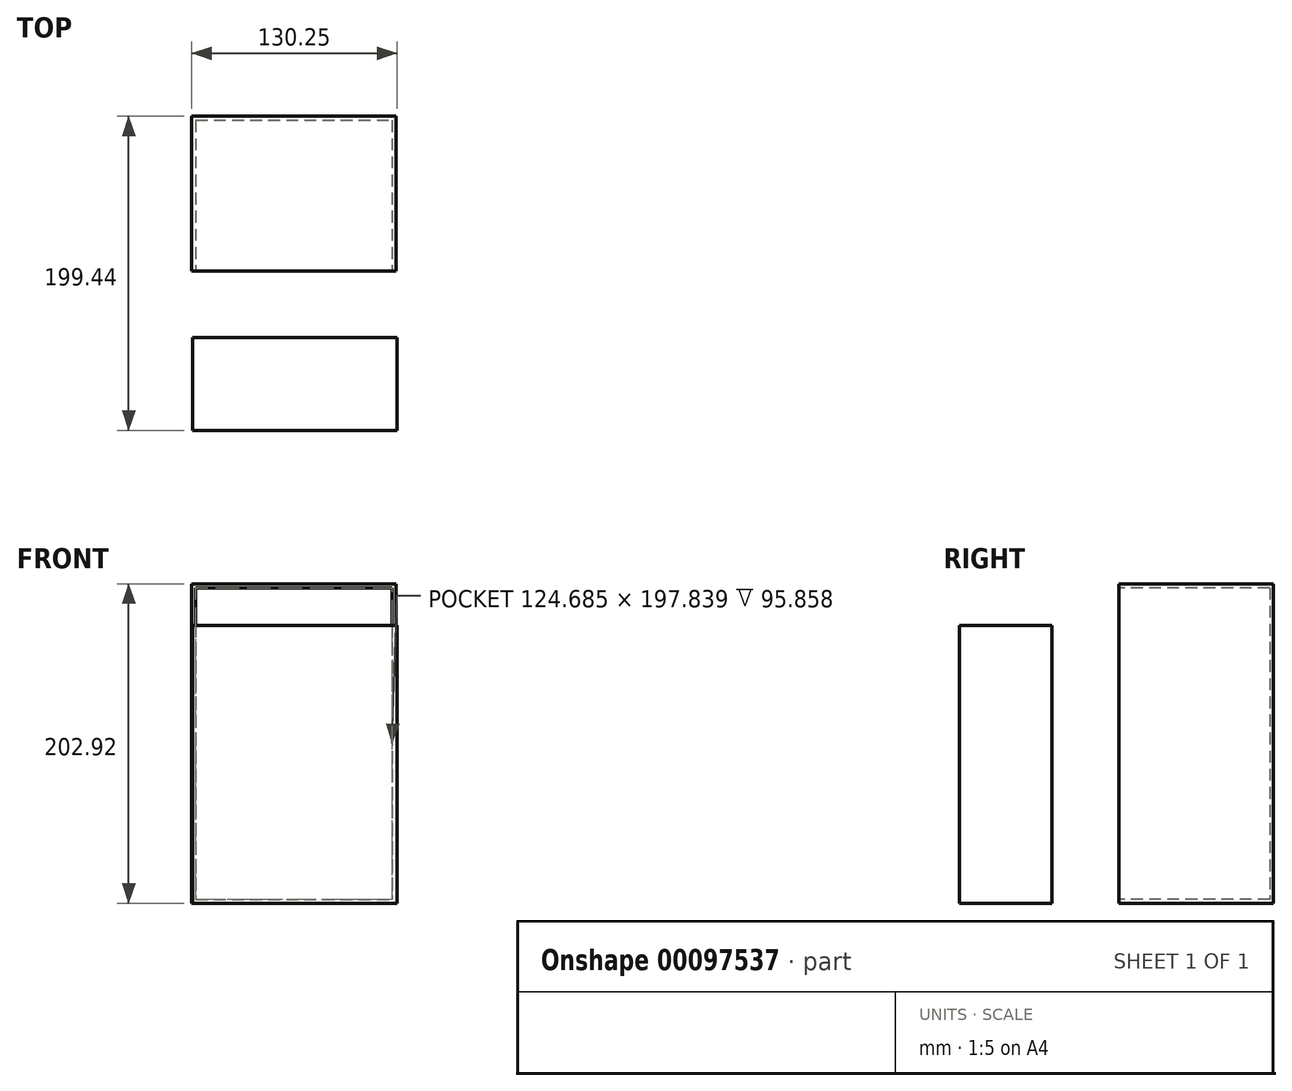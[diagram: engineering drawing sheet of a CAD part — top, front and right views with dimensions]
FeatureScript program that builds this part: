
annotation { "Feature Type Name" : "Feature", "Feature Type Description" : "" }
export const myFeature = defineFeature(function(context is Context, id is Id, definition is map)
    precondition{}
    {
        {
            var Q0;
            Q0=qCreatedBy(makeId("Top.planeOp"),FACE);
            var sketch = newSketch(context, id + "F5", { "sketchPlane" : qUnion([Q0])});
            skLineSegment(sketch, "E0.bottom", {"start": v(-37, 0) * mm, "end": v(92.76, 0) * mm});
            skLineSegment(sketch, "E0.top", {"start": v(-37, -98.4) * mm, "end": v(92.76, -98.4) * mm});
            skLineSegment(sketch, "E0.left", {"start": v(-37, 0) * mm, "end": v(-37, -98.4) * mm});
            skLineSegment(sketch, "E0.right", {"start": v(92.76, 0) * mm, "end": v(92.76, -98.4) * mm});
            skSolve(sketch);
        }
        {
            var Q0;
            Q0=makeQuery(id+"F5.imprint","IMPRINT",FACE,{"disambiguationData":[TD([[makeQuery(id+"F5.imprint","IMPRINT",EDGE,{"derivedFrom":sQuery(id+"F5.wireOp",EDGE,"E0.bottom")}),-1.0]])]});
            var sketch = newSketch(context, id + "F0", { "sketchPlane" : qUnion([Q0])});
            skSolve(sketch);
        }
        {
            var Q0;
            Q0 = qSketchRegion(id + "F0", true);
            var Q1;
            Q1=makeQuery(id+"F0.imprint","IMPRINT",FACE,{"disambiguationData":[TD([[makeQuery(id+"F0.imprint","IMPRINT",EDGE,{"derivedFrom":makeQuery(id+"F5.imprint","IMPRINT",EDGE,{"derivedFrom":sQuery(id+"F5.wireOp",EDGE,"E0.bottom")})}),-1.0]])]});
            extrude(context, id + "F1", {"entities" : qUnion([Q0, Q1]), "depth" : 202.92 * mm});
        }
        {
            var Q0;
            Q0=makeQuery(id+"F1.opExtrude","SWEPT_FACE",FACE,{"disambiguationData":[OSD([sQuery(id+"F5.wireOp",EDGE,"E0.top")])]});
            shell(context, id + "F2", {"entities" : qUnion([Q0]), "thickness" : 2.54 * mm});
        }
        {
            var Q0;
            Q0=qCreatedBy(makeId("Top.planeOp"),FACE);
            var sketch = newSketch(context, id + "F3", { "sketchPlane" : qUnion([Q0])});
            skLineSegment(sketch, "E1.bottom", {"start": v(-36.37, -199.44) * mm, "end": v(93.24, -199.44) * mm});
            skLineSegment(sketch, "E1.top", {"start": v(-36.37, -140.66) * mm, "end": v(93.24, -140.66) * mm});
            skLineSegment(sketch, "E1.left", {"start": v(-36.37, -199.44) * mm, "end": v(-36.37, -140.66) * mm});
            skLineSegment(sketch, "E1.right", {"start": v(93.24, -199.44) * mm, "end": v(93.24, -140.66) * mm});
            skSolve(sketch);
        }
        {
            var Q0;
            Q0=makeQuery(id+"F3.imprint","IMPRINT",FACE,{"disambiguationData":[TD([[makeQuery(id+"F3.imprint","IMPRINT",EDGE,{"derivedFrom":sQuery(id+"F3.wireOp",EDGE,"E1.bottom")}),1.0]])]});
            extrude(context, id + "F4", {"entities" : qUnion([Q0]), "depth" : 176.35 * mm});
        }
    });
